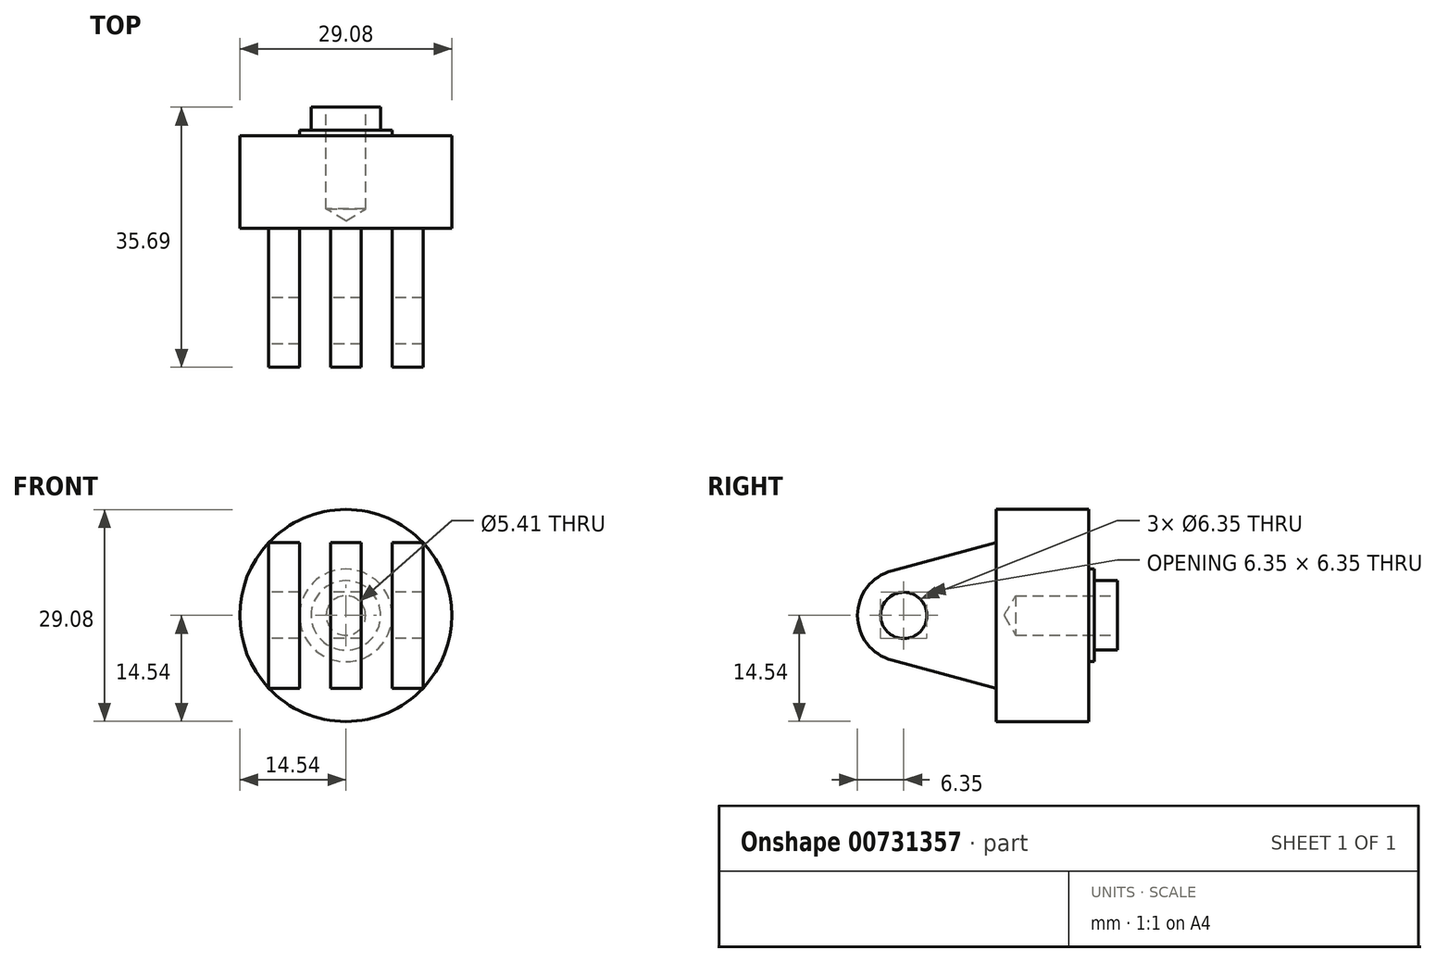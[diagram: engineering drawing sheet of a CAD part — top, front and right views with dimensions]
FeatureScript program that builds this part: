
annotation { "Feature Type Name" : "Feature", "Feature Type Description" : "" }
export const myFeature = defineFeature(function(context is Context, id is Id, definition is map)
    precondition{}
    {
        {
            var Q0;
            Q0=qCreatedBy(makeId("Right.planeOp"),FACE);
            var sketch = newSketch(context, id + "F0", { "sketchPlane" : qUnion([Q0])});
            skLineSegment(sketch, "E0", {"start": v(-14.34, -6.13) * mm, "end": v(0, -9.98) * mm});
            skLineSegment(sketch, "E1", {"start": v(0, -9.98) * mm, "end": v(0, 9.98) * mm});
            skLineSegment(sketch, "E2", {"start": v(0, 9.98) * mm, "end": v(-14.34, 6.13) * mm});
            skArc(sketch, "E3", {"start": v(-14.34, 6.13) * mm, "mid": v(-19.05, 0) * mm, "end": v(-14.34, -6.13) * mm});
            skCircle(sketch, "E4", {"center": v(-12.7, 0) * mm, "radius": 3.18 * mm});
            skSolve(sketch);
        }
        {
            var Q0;
            Q0 = qSketchRegion(id + "F0", true);
            extrude(context, id + "F1", {"entities" : qUnion([Q0]), "endBound" : BoundingType.SYMMETRIC, "depth" : 21.17 * mm, "offsetDistance" : 25.4 * mm});
        }
        {
            var Q0;
            Q0=qCreatedBy(makeId("Front.planeOp"),FACE);
            var sketch = newSketch(context, id + "F2", { "sketchPlane" : qUnion([Q0])});
            skCircle(sketch, "E5", {"center": v(0, 0) * mm, "radius": 14.54 * mm});
            skSolve(sketch);
        }
        {
            var Q0;
            Q0 = qSketchRegion(id + "F2", true);
            extrude(context, id + "F3", {"entities" : qUnion([Q0]), "operationType" : NewBodyOperationType.ADD, "oppositeDirection" : true, "depth" : 12.7 * mm, "offsetDistance" : 25.4 * mm});
        }
        {
            var Q0;
            Q0=qCreatedBy(makeId("Top.planeOp"),FACE);
            var sketch = newSketch(context, id + "F4", { "sketchPlane" : qUnion([Q0])});
            skLineSegment(sketch, "E6.bottom", {"start": v(-6.35, 0) * mm, "end": v(-2.12, 0) * mm});
            skLineSegment(sketch, "E6.top", {"start": v(-6.35, -19.05) * mm, "end": v(-2.12, -19.05) * mm});
            skLineSegment(sketch, "E6.left", {"start": v(-6.35, 0) * mm, "end": v(-6.35, -19.05) * mm});
            skLineSegment(sketch, "E6.right", {"start": v(-2.12, 0) * mm, "end": v(-2.12, -19.05) * mm});
            skLineSegment(sketch, "E7.bottom", {"start": v(2.12, 0) * mm, "end": v(6.35, 0) * mm});
            skLineSegment(sketch, "E7.top", {"start": v(2.12, -19.05) * mm, "end": v(6.35, -19.05) * mm});
            skLineSegment(sketch, "E7.left", {"start": v(2.12, 0) * mm, "end": v(2.12, -19.05) * mm});
            skLineSegment(sketch, "E7.right", {"start": v(6.35, 0) * mm, "end": v(6.35, -19.05) * mm});
            skSolve(sketch);
        }
        {
            var Q0;
            Q0 = qSketchRegion(id + "F4", true);
            extrude(context, id + "F5", {"entities" : qUnion([Q0]), "operationType" : NewBodyOperationType.REMOVE, "endBound" : BoundingType.SYMMETRIC, "oppositeDirection" : true, "depth" : 152.4 * mm, "offsetDistance" : 25.4 * mm});
        }
        {
            var Q0;
            Q0=makeQuery(id+"F3.opExtrude","CAP_FACE",FACE,{"disambiguationData":[OSD([sQuery(id+"F2.wireOp",EDGE,"E5")])],"isStart":false});
            var sketch = newSketch(context, id + "F6", { "sketchPlane" : qUnion([Q0])});
            skCircle(sketch, "E8", {"center": v(0, 0) * mm, "radius": 6.35 * mm});
            skSolve(sketch);
        }
        {
            var Q0;
            Q0 = qSketchRegion(id + "F6", true);
            extrude(context, id + "F7", {"entities" : qUnion([Q0]), "operationType" : NewBodyOperationType.ADD, "depth" : 0.76 * mm, "offsetDistance" : 25.4 * mm});
        }
        {
            var Q0;
            Q0=makeQuery(id+"F7.opExtrude","CAP_FACE",FACE,{"disambiguationData":[OSD([sQuery(id+"F6.wireOp",EDGE,"E8")])],"isStart":false});
            var sketch = newSketch(context, id + "F8", { "sketchPlane" : qUnion([Q0])});
            skPoint(sketch, "E9", {"position": v(0, 0) * mm});
            skCircle(sketch, "E10", {"center": v(0, 0) * mm, "radius": 4.76 * mm});
            skSolve(sketch);
        }
        {
            var Q0;
            Q0 = qSketchRegion(id + "F8", true);
            extrude(context, id + "F9", {"entities" : qUnion([Q0]), "operationType" : NewBodyOperationType.ADD, "depth" : 3.17 * mm, "offsetDistance" : 25.4 * mm});
        }
        {
            var Q0;
            Q0=makeQuery(id+"F9.opExtrude","CAP_FACE",FACE,{"disambiguationData":[OSD([sQuery(id+"F8.wireOp",EDGE,"E10")])],"isStart":false});
            var sketch = newSketch(context, id + "F10", { "sketchPlane" : qUnion([Q0])});
            skPoint(sketch, "E11", {"position": v(0, 0) * mm});
            skSolve(sketch);
        }
        {
            var Q0;
            Q0=sQuery(id+"F10.wireOp",VERTEX,"E11");
            var Q1;
            Q1=makeQuery(id+"F1.opExtrude","SWEPT_BODY",BODY,{"disambiguationData":[OSD([sQuery(id+"F0.wireOp",EDGE,"E0"),sQuery(id+"F0.wireOp",EDGE,"E1"),sQuery(id+"F0.wireOp",EDGE,"E2"),sQuery(id+"F0.wireOp",EDGE,"E3"),sQuery(id+"F0.wireOp",EDGE,"E4")])]});
            hole(context, id + "F11", {"style" : HoleStyle.SIMPLE, "endStyle" : HoleEndStyle.BLIND, "standardTappedOrClearance" : lookupTablePath({ "standard" : "ANSI", "engagement" : "75%", "pitch" : "28 tpi", "size" : "1/4", "type" : "Tapped" }), "standardBlindInLast" : lookupTablePath({ "standard" : "ANSI", "engagement" : "75%", "pitch" : "28 tpi", "size" : "1/4", "type" : "Tapped" }), "holeDiameter" : 5.4 * mm, "majorDiameter" : 6.35 * mm, "showTappedDepth" : true, "holeDepth" : 13.97 * mm, "isTappedThrough" : true, "tappedDepth" : 11.25 * mm, "tapClearance" : 3, "locations" : qUnion([Q0]), "scope" : qUnion([Q1])});
        }
    });
